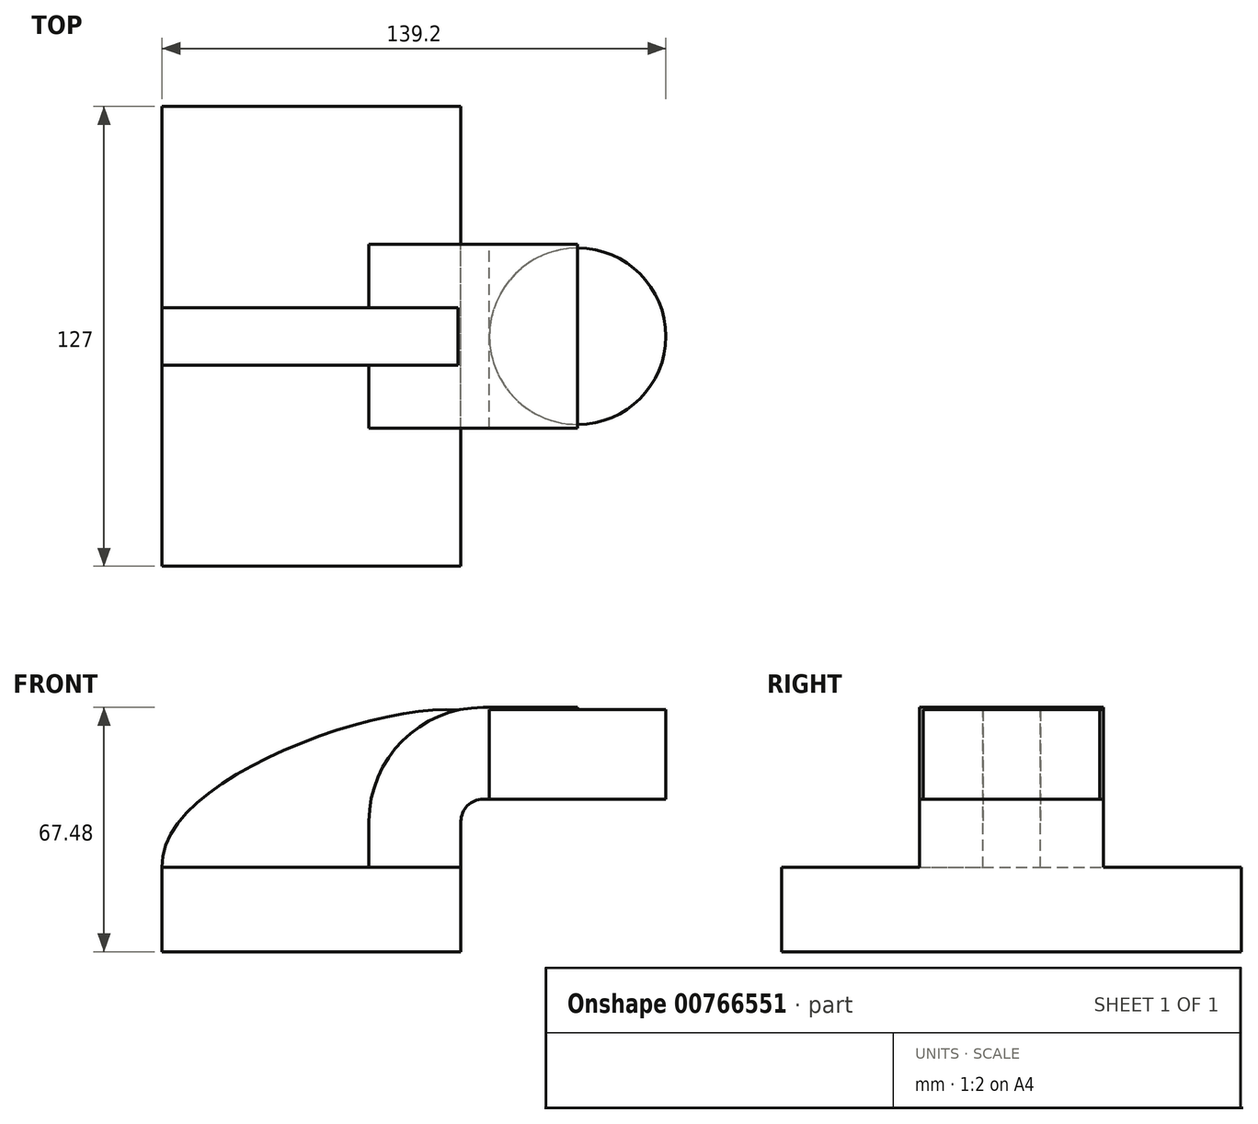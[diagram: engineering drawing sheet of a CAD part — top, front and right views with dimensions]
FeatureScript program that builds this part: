
annotation { "Feature Type Name" : "Feature", "Feature Type Description" : "" }
export const myFeature = defineFeature(function(context is Context, id is Id, definition is map)
    precondition{}
    {
        {
            var Q0;
            Q0=qCreatedBy(makeId("Front.planeOp"),FACE);
            var sketch = newSketch(context, id + "F0", { "sketchPlane" : qUnion([Q0])});
            skLineSegment(sketch, "E0.bottom", {"start": v(-41.28, 11.64) * mm, "end": v(41.28, 11.64) * mm});
            skLineSegment(sketch, "E0.top", {"start": v(-41.28, -11.64) * mm, "end": v(41.28, -11.64) * mm});
            skLineSegment(sketch, "E0.left", {"start": v(-41.28, 11.64) * mm, "end": v(-41.28, -11.64) * mm});
            skLineSegment(sketch, "E0.right", {"start": v(41.28, 11.64) * mm, "end": v(41.28, -11.64) * mm});
            skPoint(sketch, "E0.middle", {"position": v(0, 0) * mm});
            skLineSegment(sketch, "E1.bottom", {"start": v(49.16, 55.19) * mm, "end": v(92.34, 55.19) * mm});
            skLineSegment(sketch, "E1.top", {"start": v(49.16, 22.17) * mm, "end": v(92.34, 22.17) * mm});
            skLineSegment(sketch, "E1.left", {"start": v(49.16, 55.19) * mm, "end": v(49.16, 22.17) * mm});
            skLineSegment(sketch, "E1.right", {"start": v(92.34, 55.19) * mm, "end": v(92.34, 22.17) * mm});
            skPoint(sketch, "E1.middle", {"position": v(70.75, 38.68) * mm});
            skLineSegment(sketch, "E2", {"start": v(41.28, 11.64) * mm, "end": v(41.28, 24.34) * mm});
            skArc(sketch, "E3", {"start": v(41.28, 24.34) * mm, "mid": v(43.06, 28.66) * mm, "end": v(47.38, 30.44) * mm});
            skLineSegment(sketch, "E4", {"start": v(47.38, 30.44) * mm, "end": v(73.53, 30.44) * mm});
            skLineSegment(sketch, "E5.0", {"start": v(47.38, 55.84) * mm, "end": v(73.53, 55.84) * mm});
            skArc(sketch, "E5.1", {"start": v(15.88, 24.34) * mm, "mid": v(25.1, 46.62) * mm, "end": v(47.38, 55.84) * mm});
            skLineSegment(sketch, "E5.2", {"start": v(15.88, 11.64) * mm, "end": v(15.88, 24.34) * mm});
            skLineSegment(sketch, "E6", {"start": v(73.53, 55.84) * mm, "end": v(73.53, 30.44) * mm});
            skLineSegment(sketch, "E7", {"start": v(15.88, 11.64) * mm, "end": v(41.28, 11.64) * mm});
            skFitSpline(sketch, "E8", {"points": [v(-41.28, 11.64) * mm, v(40.41, 55.06) * mm], "startDerivative": vector(-4.61, 71.4) * mm, "endDerivative": vector(70.43, -5.9) * mm});
            skSolve(sketch);
        }
        {
            var Q0;
            Q0=makeQuery(id+"F0.imprint","IMPRINT",FACE,{"disambiguationData":[TD([[makeQuery(id+"F0.imprint","IMPRINT",EDGE,{"derivedFrom":sQuery(id+"F0.wireOp",EDGE,"E0.bottom")}),-1.0]])]});
            extrude(context, id + "F1", {"entities" : qUnion([Q0]), "endBound" : BoundingType.SYMMETRIC, "depth" : 127 * mm, "offsetDistance" : 25.4 * mm});
        }
        {
            var Q0;
            Q0=makeQuery(id+"F0.imprint","IMPRINT",FACE,{"disambiguationData":[TD([[makeQuery(id+"F0.imprint","IMPRINT",EDGE,{"derivedFrom":sQuery(id+"F0.wireOp",EDGE,"E2")}),1.0]])]});
            extrude(context, id + "F2", {"entities" : qUnion([Q0]), "operationType" : NewBodyOperationType.ADD, "endBound" : BoundingType.SYMMETRIC, "depth" : 50.8 * mm, "offsetDistance" : 25.4 * mm});
        }
        {
            var Q0;
            Q0=makeQuery(id+"F0.imprint","IMPRINT",FACE,{"disambiguationData":[TD([[makeQuery(id+"F0.imprint","IMPRINT",EDGE,{"derivedFrom":sQuery(id+"F0.wireOp",EDGE,"E0.bottom")}),1.0]])]});
            extrude(context, id + "F3", {"entities" : qUnion([Q0]), "operationType" : NewBodyOperationType.ADD, "endBound" : BoundingType.SYMMETRIC, "depth" : 15.88 * mm, "offsetDistance" : 25.4 * mm});
        }
        {
            var Q0;
            {var subQ0=sQuery(id+"F0.wireOp",EDGE,"E1.left");var subQ1=sQuery(id+"F0.wireOp",EDGE,"E1.bottom");var subQ2=makeQuery(id+"F0.imprint","INTERSECT",VERTEX,{"derivedFrom":[subQ1,subQ0]});Q0=makeQuery(id+"F0.imprint","IMPRINT",FACE,{"disambiguationData":[TD([[makeQuery(id+"F0.imprint","IMPRINT",EDGE,{"disambiguationData":[TD([[subQ2,-1.0]])],"derivedFrom":subQ1}),-1.0]])]});}
            var Q1;
            Q1=sQuery(id+"F0.wireOp",EDGE,"E6");
            revolve(context, id + "F4", {"surfaceOperationType" : NewSurfaceOperationType.NEW, "entities" : qUnion([Q0]), "axis" : qUnion([Q1]), "revolveType" : RevolveType.FULL});
        }
    });
